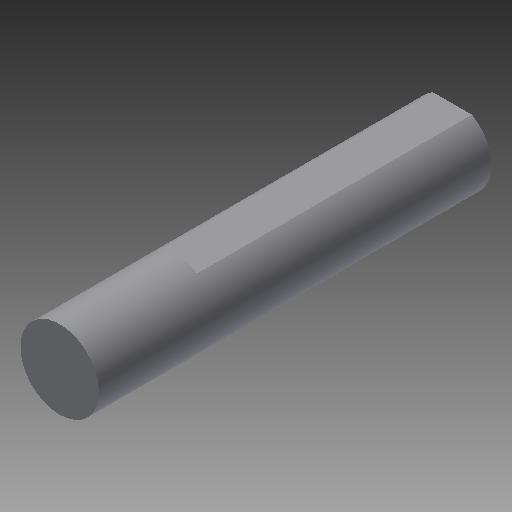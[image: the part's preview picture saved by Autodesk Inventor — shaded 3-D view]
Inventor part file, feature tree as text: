
AUTODESK INVENTOR PART (.ipt)
format: ipt  version: 2017 (Build 210142000, 142)  size: 91,136 bytes
history: native  units: in
note: dims shown in document units (in); Inventor stores cm internally (conversion verified against a paired STEP export)
features: extrude x2, sketch x2
ambient origin geometry x8: Origin, YZ Plane, XZ Plane, XY Plane, X Axis, Y Axis, Z Axis, Center Point
bodies: Solid1 (feature_tree)
feature tree (4):
  extrude  "Extrusion1"  Depth=0.125in
  extrude  "Extrusion2"  Depth=0.375in TaperAngle=0.0deg
  sketch  "Sketch1"  dims[d0=0.25in d1=0.125in]
  sketch  "Sketch2"  dims[d2=1.25in d3=0.0in d4=0.375in d5=0.0in]
